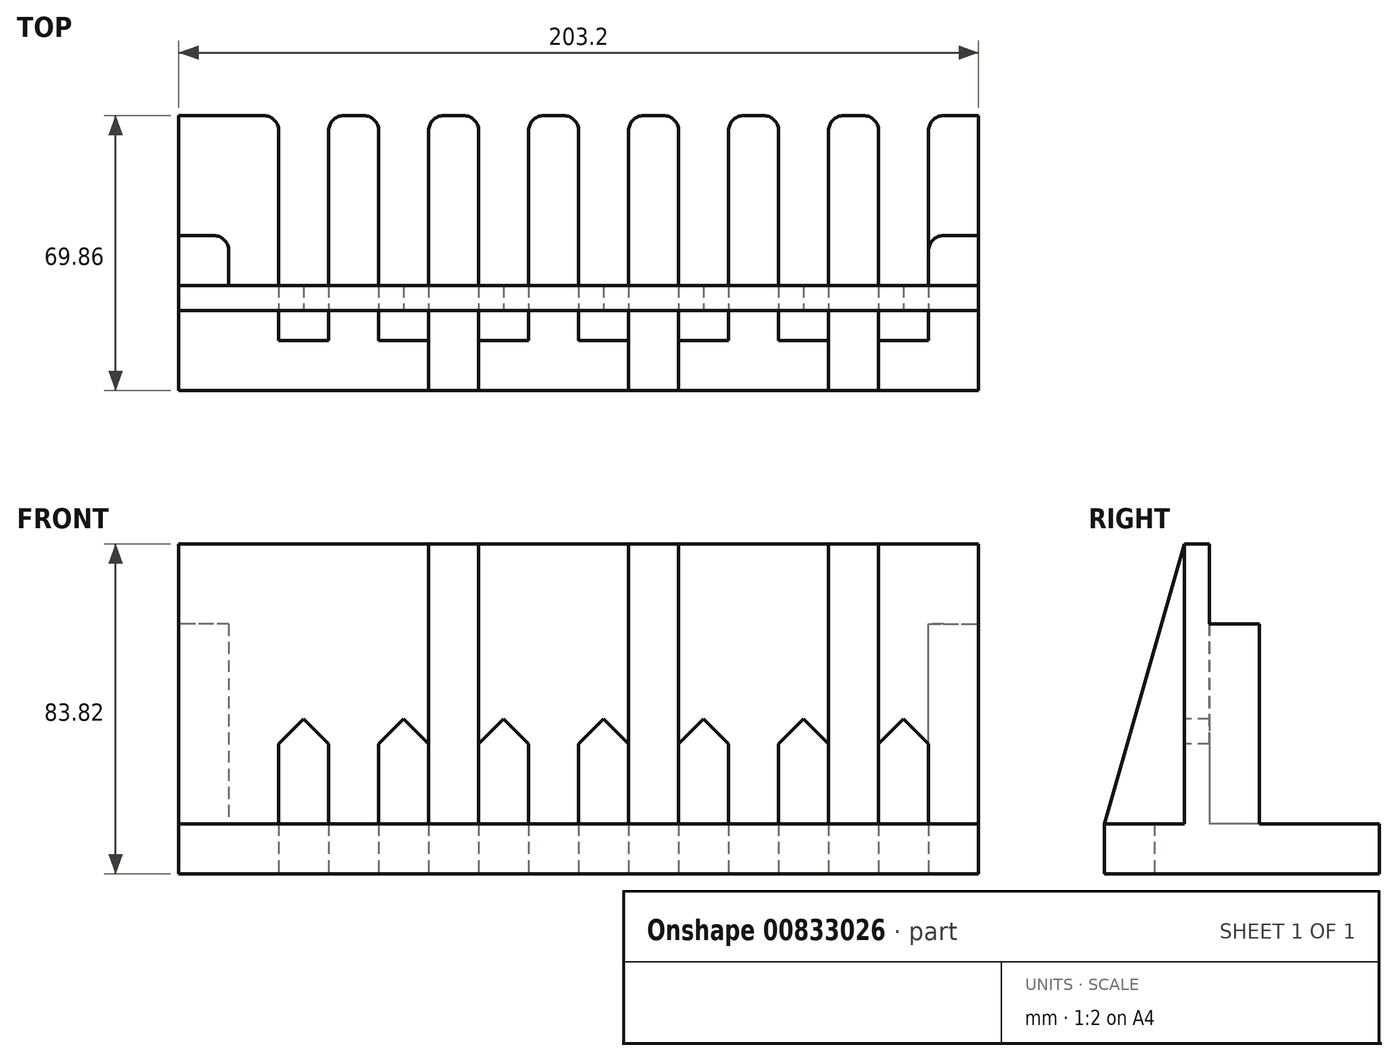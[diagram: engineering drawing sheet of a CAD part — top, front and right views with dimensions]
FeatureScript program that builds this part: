
annotation { "Feature Type Name" : "Feature", "Feature Type Description" : "" }
export const myFeature = defineFeature(function(context is Context, id is Id, definition is map)
    precondition{}
    {
        {
            var Q0;
            Q0=qCreatedBy(makeId("Top.planeOp"),FACE);
            var sketch = newSketch(context, id + "F0", { "sketchPlane" : qUnion([Q0])});
            skLineSegment(sketch, "E0.bottom", {"start": v(101.6, 34.93) * mm, "end": v(88.9, 34.93) * mm});
            skLineSegment(sketch, "E0.top", {"start": v(101.6, -34.92) * mm, "end": v(-101.6, -34.93) * mm});
            skLineSegment(sketch, "E0.left", {"start": v(101.6, 34.93) * mm, "end": v(101.6, -34.92) * mm});
            skLineSegment(sketch, "E0.right", {"start": v(-101.6, 34.92) * mm, "end": v(-101.6, -34.93) * mm});
            skPoint(sketch, "E0.middle", {"position": v(0, 0) * mm});
            skLineSegment(sketch, "E1.top", {"start": v(88.9, -22.23) * mm, "end": v(76.2, -22.23) * mm});
            skLineSegment(sketch, "E1.left", {"start": v(88.9, 34.93) * mm, "end": v(88.9, -22.23) * mm});
            skLineSegment(sketch, "E1.right", {"start": v(76.2, 34.93) * mm, "end": v(76.2, -22.23) * mm});
            skLineSegment(sketch, "E2.top", {"start": v(63.5, -22.23) * mm, "end": v(50.8, -22.23) * mm});
            skLineSegment(sketch, "E2.left", {"start": v(63.5, 34.93) * mm, "end": v(63.5, -22.23) * mm});
            skLineSegment(sketch, "E2.right", {"start": v(50.8, 34.93) * mm, "end": v(50.8, -22.23) * mm});
            skLineSegment(sketch, "E3.top", {"start": v(38.1, -22.22) * mm, "end": v(25.4, -22.22) * mm});
            skLineSegment(sketch, "E3.left", {"start": v(38.1, 34.93) * mm, "end": v(38.1, -22.22) * mm});
            skLineSegment(sketch, "E3.right", {"start": v(25.4, 34.93) * mm, "end": v(25.4, -22.23) * mm});
            skLineSegment(sketch, "E4.trimOffspring", {"start": v(50.8, 34.93) * mm, "end": v(38.1, 34.93) * mm});
            skLineSegment(sketch, "E5.trimOffspring", {"start": v(25.4, 34.93) * mm, "end": v(12.7, 34.93) * mm});
            skLineSegment(sketch, "E6.trimOffspring", {"start": v(76.2, 34.93) * mm, "end": v(63.5, 34.93) * mm});
            skLineSegment(sketch, "E7.top", {"start": v(12.7, -22.22) * mm, "end": v(0, -22.23) * mm});
            skLineSegment(sketch, "E7.left", {"start": v(12.7, 34.93) * mm, "end": v(12.7, -22.22) * mm});
            skLineSegment(sketch, "E7.right", {"start": v(0, 34.93) * mm, "end": v(0, -22.23) * mm});
            skLineSegment(sketch, "E8.top", {"start": v(-12.7, -22.22) * mm, "end": v(-25.4, -22.23) * mm});
            skLineSegment(sketch, "E8.left", {"start": v(-12.7, 34.93) * mm, "end": v(-12.7, -22.23) * mm});
            skLineSegment(sketch, "E8.right", {"start": v(-25.4, 34.93) * mm, "end": v(-25.4, -22.23) * mm});
            skLineSegment(sketch, "E9.top", {"start": v(-38.1, -22.22) * mm, "end": v(-50.8, -22.23) * mm});
            skLineSegment(sketch, "E9.left", {"start": v(-38.1, 34.93) * mm, "end": v(-38.1, -22.22) * mm});
            skLineSegment(sketch, "E9.right", {"start": v(-50.8, 34.92) * mm, "end": v(-50.8, -22.23) * mm});
            skLineSegment(sketch, "E10.trimOffspring", {"start": v(0, 34.93) * mm, "end": v(-12.7, 34.93) * mm});
            skLineSegment(sketch, "E11.trimOffspring", {"start": v(-25.4, 34.93) * mm, "end": v(-38.1, 34.93) * mm});
            skLineSegment(sketch, "E12.trimOffspring", {"start": v(-50.8, 34.92) * mm, "end": v(-63.5, 34.92) * mm});
            skLineSegment(sketch, "E13.bottom", {"start": v(-101.6, 34.92) * mm, "end": v(-88.9, 34.92) * mm});
            skLineSegment(sketch, "E13.top", {"start": v(-101.6, -22.23) * mm, "end": v(-88.9, -22.22) * mm});
            skLineSegment(sketch, "E13.left", {"start": v(-101.6, 34.92) * mm, "end": v(-101.6, -22.23) * mm});
            skLineSegment(sketch, "E13.right", {"start": v(-88.9, 34.92) * mm, "end": v(-88.9, -22.22) * mm});
            skLineSegment(sketch, "E14.top", {"start": v(-63.5, -22.22) * mm, "end": v(-76.2, -22.22) * mm});
            skLineSegment(sketch, "E14.left", {"start": v(-63.5, 34.92) * mm, "end": v(-63.5, -22.22) * mm});
            skLineSegment(sketch, "E14.right", {"start": v(-76.2, 34.92) * mm, "end": v(-76.2, -22.22) * mm});
            skLineSegment(sketch, "E15.trimOffspring", {"start": v(-76.2, 34.92) * mm, "end": v(-101.6, 34.92) * mm});
            skSolve(sketch);
        }
        {
            var Q0;
            Q0=makeQuery(id+"F0.imprint","IMPRINT",FACE,{"disambiguationData":[TD([[makeQuery(id+"F0.imprint","IMPRINT",EDGE,{"derivedFrom":sQuery(id+"F0.wireOp",EDGE,"E0.bottom")}),1.0]])]});
            var Q1;
            Q1=makeQuery(id+"F0.imprint","IMPRINT",FACE,{"disambiguationData":[TD([[makeQuery(id+"F0.imprint","IMPRINT",EDGE,{"derivedFrom":sQuery(id+"F0.wireOp",EDGE,"E13.top")}),1.0]])]});
            extrude(context, id + "F1", {"entities" : qUnion([Q0, Q1]), "depth" : 12.7 * mm, "offsetDistance" : 25.4 * mm});
        }
        {
            var Q0;
            Q0=makeQuery(id+"F1.opExtrude","CAP_FACE",FACE,{"disambiguationData":[OSD([sQuery(id+"F0.wireOp",EDGE,"E0.bottom"),sQuery(id+"F0.wireOp",EDGE,"E0.top"),sQuery(id+"F0.wireOp",EDGE,"E0.left"),sQuery(id+"F0.wireOp",EDGE,"E0.right"),sQuery(id+"F0.wireOp",EDGE,"E1.top"),sQuery(id+"F0.wireOp",EDGE,"E1.left"),sQuery(id+"F0.wireOp",EDGE,"E1.right"),sQuery(id+"F0.wireOp",EDGE,"E2.top"),sQuery(id+"F0.wireOp",EDGE,"E2.left"),sQuery(id+"F0.wireOp",EDGE,"E2.right"),sQuery(id+"F0.wireOp",EDGE,"E3.top"),sQuery(id+"F0.wireOp",EDGE,"E3.left"),sQuery(id+"F0.wireOp",EDGE,"E3.right"),sQuery(id+"F0.wireOp",EDGE,"E4.trimOffspring"),sQuery(id+"F0.wireOp",EDGE,"E5.trimOffspring"),sQuery(id+"F0.wireOp",EDGE,"E6.trimOffspring"),sQuery(id+"F0.wireOp",EDGE,"E7.top"),sQuery(id+"F0.wireOp",EDGE,"E7.left"),sQuery(id+"F0.wireOp",EDGE,"E7.right"),sQuery(id+"F0.wireOp",EDGE,"E8.top"),sQuery(id+"F0.wireOp",EDGE,"E8.left"),sQuery(id+"F0.wireOp",EDGE,"E8.right"),sQuery(id+"F0.wireOp",EDGE,"E9.top"),sQuery(id+"F0.wireOp",EDGE,"E9.left"),sQuery(id+"F0.wireOp",EDGE,"E9.right"),sQuery(id+"F0.wireOp",EDGE,"E10.trimOffspring"),sQuery(id+"F0.wireOp",EDGE,"E11.trimOffspring"),sQuery(id+"F0.wireOp",EDGE,"E12.trimOffspring")])],"isStart":false});
            var sketch = newSketch(context, id + "F2", { "sketchPlane" : qUnion([Q0])});
            skLineSegment(sketch, "E16.bottom", {"start": v(-101.6, -8.26) * mm, "end": v(101.6, -8.25) * mm});
            skLineSegment(sketch, "E16.top", {"start": v(-101.6, -14.6) * mm, "end": v(101.6, -14.6) * mm});
            skLineSegment(sketch, "E16.left", {"start": v(-101.6, -8.26) * mm, "end": v(-101.6, -14.6) * mm});
            skLineSegment(sketch, "E16.right", {"start": v(101.6, -8.25) * mm, "end": v(101.6, -14.6) * mm});
            skSolve(sketch);
        }
        {
            var Q0;
            {var subQ0=sQuery(id+"F2.wireOp",EDGE,"E16.left");Q0=makeQuery(id+"F2.imprint","IMPRINT",FACE,{"disambiguationData":[TD([[makeQuery(id+"F2.imprint","IMPRINT",EDGE,{"derivedFrom":subQ0}),1.0]])]});}
            var Q1;
            {var subQ0=sQuery(id+"F2.wireOp",EDGE,"E16.bottom");var subQ1=makeQuery(id+"F1.opExtrude","CAP_EDGE",EDGE,{"disambiguationData":[OSD([sQuery(id+"F0.wireOp",EDGE,"E9.left")])],"isStart":false});var subQ2=makeQuery(id+"F2.imprint","INTERSECT",VERTEX,{"derivedFrom":[subQ1,subQ0]});Q1=makeQuery(id+"F2.imprint","IMPRINT",FACE,{"disambiguationData":[TD([[makeQuery(id+"F2.imprint","IMPRINT",EDGE,{"disambiguationData":[TD([[subQ2,-1.0]])],"derivedFrom":subQ0}),-1.0]])]});}
            var Q2;
            {var subQ0=sQuery(id+"F2.wireOp",EDGE,"E16.bottom");var subQ1=makeQuery(id+"F1.opExtrude","CAP_EDGE",EDGE,{"disambiguationData":[OSD([sQuery(id+"F0.wireOp",EDGE,"E8.left")])],"isStart":false});var subQ2=makeQuery(id+"F2.imprint","INTERSECT",VERTEX,{"derivedFrom":[subQ1,subQ0]});Q2=makeQuery(id+"F2.imprint","IMPRINT",FACE,{"disambiguationData":[TD([[makeQuery(id+"F2.imprint","IMPRINT",EDGE,{"disambiguationData":[TD([[subQ2,-1.0]])],"derivedFrom":subQ0}),-1.0]])]});}
            var Q3;
            {var subQ0=sQuery(id+"F2.wireOp",EDGE,"E16.bottom");var subQ1=makeQuery(id+"F1.opExtrude","CAP_EDGE",EDGE,{"disambiguationData":[OSD([sQuery(id+"F0.wireOp",EDGE,"E7.left")])],"isStart":false});var subQ2=makeQuery(id+"F2.imprint","INTERSECT",VERTEX,{"derivedFrom":[subQ1,subQ0]});Q3=makeQuery(id+"F2.imprint","IMPRINT",FACE,{"disambiguationData":[TD([[makeQuery(id+"F2.imprint","IMPRINT",EDGE,{"disambiguationData":[TD([[subQ2,-1.0]])],"derivedFrom":subQ0}),-1.0]])]});}
            var Q4;
            {var subQ0=sQuery(id+"F2.wireOp",EDGE,"E16.bottom");var subQ1=makeQuery(id+"F1.opExtrude","CAP_EDGE",EDGE,{"disambiguationData":[OSD([sQuery(id+"F0.wireOp",EDGE,"E3.left")])],"isStart":false});var subQ2=makeQuery(id+"F2.imprint","INTERSECT",VERTEX,{"derivedFrom":[subQ1,subQ0]});Q4=makeQuery(id+"F2.imprint","IMPRINT",FACE,{"disambiguationData":[TD([[makeQuery(id+"F2.imprint","IMPRINT",EDGE,{"disambiguationData":[TD([[subQ2,-1.0]])],"derivedFrom":subQ0}),-1.0]])]});}
            var Q5;
            {var subQ0=sQuery(id+"F2.wireOp",EDGE,"E16.bottom");var subQ1=makeQuery(id+"F1.opExtrude","CAP_EDGE",EDGE,{"disambiguationData":[OSD([sQuery(id+"F0.wireOp",EDGE,"E2.left")])],"isStart":false});var subQ2=makeQuery(id+"F2.imprint","INTERSECT",VERTEX,{"derivedFrom":[subQ1,subQ0]});Q5=makeQuery(id+"F2.imprint","IMPRINT",FACE,{"disambiguationData":[TD([[makeQuery(id+"F2.imprint","IMPRINT",EDGE,{"disambiguationData":[TD([[subQ2,-1.0]])],"derivedFrom":subQ0}),-1.0]])]});}
            var Q6;
            {var subQ0=sQuery(id+"F2.wireOp",EDGE,"E16.right");Q6=makeQuery(id+"F2.imprint","IMPRINT",FACE,{"disambiguationData":[TD([[makeQuery(id+"F2.imprint","IMPRINT",EDGE,{"derivedFrom":subQ0}),-1.0]])]});}
            var Q7;
            {var subQ0=sQuery(id+"F2.wireOp",EDGE,"E16.bottom");var subQ1=makeQuery(id+"F1.opExtrude","CAP_EDGE",EDGE,{"disambiguationData":[OSD([sQuery(id+"F0.wireOp",EDGE,"E14.left")])],"isStart":false});var subQ2=makeQuery(id+"F2.imprint","INTERSECT",VERTEX,{"derivedFrom":[subQ1,subQ0]});Q7=makeQuery(id+"F2.imprint","IMPRINT",FACE,{"disambiguationData":[TD([[makeQuery(id+"F2.imprint","IMPRINT",EDGE,{"disambiguationData":[TD([[subQ2,-1.0]])],"derivedFrom":subQ0}),-1.0]])]});}
            extrude(context, id + "F3", {"entities" : qUnion([Q0, Q1, Q2, Q3, Q4, Q5, Q6, Q7]), "operationType" : NewBodyOperationType.ADD, "depth" : 20.32 * mm, "offsetDistance" : 25.4 * mm});
        }
        {
            var Q0;
            Q0=makeQuery(id+"F3.opExtrude","CAP_FACE",FACE,{"disambiguationData":[OSD([sQuery(id+"F0.wireOp",EDGE,"E9.right"),sQuery(id+"F2.wireOp",EDGE,"E16.bottom"),sQuery(id+"F2.wireOp",EDGE,"E16.top"),sQuery(id+"F2.wireOp",EDGE,"E16.left")])],"isStart":false});
            var sketch = newSketch(context, id + "F4", { "sketchPlane" : qUnion([Q0])});
            skLineSegment(sketch, "E17.bottom", {"start": v(-101.6, -8.25) * mm, "end": v(101.6, -8.25) * mm});
            skLineSegment(sketch, "E17.top", {"start": v(-101.6, -14.6) * mm, "end": v(101.6, -14.6) * mm});
            skLineSegment(sketch, "E17.left", {"start": v(-101.6, -8.25) * mm, "end": v(-101.6, -14.6) * mm});
            skLineSegment(sketch, "E17.right", {"start": v(101.6, -8.25) * mm, "end": v(101.6, -14.6) * mm});
            skSolve(sketch);
        }
        {
            var Q0;
            {var subQ0=sQuery(id+"F4.wireOp",EDGE,"E17.left");Q0=makeQuery(id+"F4.imprint","IMPRINT",FACE,{"disambiguationData":[TD([[makeQuery(id+"F4.imprint","IMPRINT",EDGE,{"derivedFrom":subQ0}),1.0]])]});}
            var Q1;
            {var subQ2=sQuery(id+"F4.wireOp",EDGE,"E17.right");Q1=makeQuery(id+"F4.imprint","IMPRINT",FACE,{"disambiguationData":[TD([[makeQuery(id+"F4.imprint","IMPRINT",EDGE,{"derivedFrom":subQ2}),-1.0]])]});}
            var Q2;
            {var subQ2=makeQuery(id+"F3.opExtrude","CAP_EDGE",EDGE,{"disambiguationData":[OSD([sQuery(id+"F0.wireOp",EDGE,"E9.right")])],"isStart":false});Q2=makeQuery(id+"F4.imprint","IMPRINT",FACE,{"disambiguationData":[TD([[makeQuery(id+"F4.imprint","IMPRINT",EDGE,{"derivedFrom":subQ2}),-1.0]])]});}
            var Q3;
            {var subQ2=makeQuery(id+"F3.opExtrude","CAP_EDGE",EDGE,{"disambiguationData":[OSD([sQuery(id+"F0.wireOp",EDGE,"E14.left")])],"isStart":false});Q3=makeQuery(id+"F4.imprint","IMPRINT",FACE,{"disambiguationData":[TD([[makeQuery(id+"F4.imprint","IMPRINT",EDGE,{"derivedFrom":subQ2}),-1.0]])]});}
            extrude(context, id + "F5", {"entities" : qUnion([Q0, Q1, Q2, Q3]), "operationType" : NewBodyOperationType.ADD, "depth" : 50.8 * mm, "offsetDistance" : 25.4 * mm});
        }
        {
            var Q0;
            Q0=makeQuery(id+"F5.boolean.opBoolean","MERGE",FACE,{"derivedFrom":[makeQuery(id+"F3.boolean.opBoolean","MERGE",FACE,{"derivedFrom":[makeQuery(id+"F1.opExtrude","SWEPT_FACE",FACE,{"disambiguationData":[OSD([sQuery(id+"F0.wireOp",EDGE,"E0.right")])]}),makeQuery(id+"F3.opExtrude","SWEPT_FACE",FACE,{"disambiguationData":[OSD([sQuery(id+"F2.wireOp",EDGE,"E16.left")])]})]}),makeQuery(id+"F5.opExtrude","SWEPT_FACE",FACE,{"disambiguationData":[OSD([sQuery(id+"F4.wireOp",EDGE,"E17.left")])]})]});
            var sketch = newSketch(context, id + "F6", { "sketchPlane" : qUnion([Q0])});
            skLineSegment(sketch, "E18.bottom", {"start": v(8.25, 12.7) * mm, "end": v(-4.45, 12.7) * mm});
            skLineSegment(sketch, "E18.top", {"start": v(8.25, 63.5) * mm, "end": v(-4.45, 63.5) * mm});
            skLineSegment(sketch, "E18.left", {"start": v(8.25, 12.7) * mm, "end": v(8.25, 63.5) * mm});
            skLineSegment(sketch, "E18.right", {"start": v(-4.45, 12.7) * mm, "end": v(-4.45, 63.5) * mm});
            skSolve(sketch);
        }
        {
            var Q0;
            Q0=makeQuery(id+"F6.imprint","IMPRINT",FACE,{"disambiguationData":[TD([[makeQuery(id+"F6.imprint","IMPRINT",EDGE,{"derivedFrom":sQuery(id+"F6.wireOp",EDGE,"E18.bottom")}),1.0]])]});
            var Q1;
            Q1=makeQuery(id+"F6.imprint","IMPRINT",FACE,{"disambiguationData":[TD([[makeQuery(id+"F6.imprint","IMPRINT",EDGE,{"derivedFrom":sQuery(id+"F6.wireOp",EDGE,"ogDCGRYY-HDVT-Hkr0-qh3N-PnepQPiMfiLJ")}),-1.0]])]});
            extrude(context, id + "F7", {"entities" : qUnion([Q0, Q1]), "operationType" : NewBodyOperationType.ADD, "oppositeDirection" : true, "depth" : 12.7 * mm, "offsetDistance" : 25.4 * mm});
        }
        {
            var Q0;
            {var subQ0=sQuery(id+"F0.wireOp",EDGE,"E8.right");Q0=makeQuery(id+"F3.boolean.opBoolean","MERGE",FACE,{"derivedFrom":[makeQuery(id+"F1.opExtrude","SWEPT_FACE",FACE,{"disambiguationData":[OSD([subQ0])]}),makeQuery(id+"F3.opExtrude","SWEPT_FACE",FACE,{"disambiguationData":[OSD([subQ0])]})]});}
            var sketch = newSketch(context, id + "F8", { "sketchPlane" : qUnion([Q0])});
            skLineSegment(sketch, "E19", {"start": v(-14.6, 83.82) * mm, "end": v(-34.93, 12.7) * mm});
            skLineSegment(sketch, "E20", {"start": v(-34.92, 12.7) * mm, "end": v(-14.6, 12.7) * mm});
            skLineSegment(sketch, "E21", {"start": v(-14.6, 12.7) * mm, "end": v(-14.6, 83.82) * mm});
            skSolve(sketch);
        }
        {
            var Q0;
            {var subQ3=sQuery(id+"F8.wireOp",EDGE,"E19");Q0=makeQuery(id+"F8.imprint","IMPRINT",FACE,{"disambiguationData":[TD([[makeQuery(id+"F8.imprint","IMPRINT",EDGE,{"derivedFrom":subQ3}),1.0]])]});}
            var Q1;
            {var subQ0=sQuery(id+"F0.wireOp",EDGE,"E9.left");Q1=makeQuery(id+"F3.boolean.opBoolean","MERGE",FACE,{"derivedFrom":[makeQuery(id+"F1.opExtrude","SWEPT_FACE",FACE,{"disambiguationData":[OSD([subQ0])]}),makeQuery(id+"F3.opExtrude","SWEPT_FACE",FACE,{"disambiguationData":[OSD([subQ0])]})]});}
            extrude(context, id + "F9", {"entities" : qUnion([Q0]), "operationType" : NewBodyOperationType.ADD, "endBound" : BoundingType.UP_TO_SURFACE, "oppositeDirection" : true, "depth" : 25.4 * mm, "endBoundEntityFace" : qUnion([Q1]), "offsetDistance" : 25.4 * mm});
        }
        {
            var Q0;
            {var subQ0=sQuery(id+"F0.wireOp",EDGE,"E3.right");Q0=makeQuery(id+"F3.boolean.opBoolean","MERGE",FACE,{"derivedFrom":[makeQuery(id+"F1.opExtrude","SWEPT_FACE",FACE,{"disambiguationData":[OSD([subQ0])]}),makeQuery(id+"F3.opExtrude","SWEPT_FACE",FACE,{"disambiguationData":[OSD([subQ0])]})]});}
            var sketch = newSketch(context, id + "F10", { "sketchPlane" : qUnion([Q0])});
            skLineSegment(sketch, "E22", {"start": v(-14.6, 83.82) * mm, "end": v(-34.93, 12.7) * mm});
            skLineSegment(sketch, "E23", {"start": v(-34.92, 12.7) * mm, "end": v(-14.6, 12.7) * mm});
            skLineSegment(sketch, "E24", {"start": v(-14.6, 12.7) * mm, "end": v(-14.6, 83.82) * mm});
            skSolve(sketch);
        }
        {
            var Q0;
            {var subQ3=sQuery(id+"F10.wireOp",EDGE,"E22");Q0=makeQuery(id+"F10.imprint","IMPRINT",FACE,{"disambiguationData":[TD([[makeQuery(id+"F10.imprint","IMPRINT",EDGE,{"derivedFrom":subQ3}),1.0]])]});}
            var Q1;
            {var subQ0=sQuery(id+"F0.wireOp",EDGE,"E7.left");Q1=makeQuery(id+"F3.boolean.opBoolean","MERGE",FACE,{"derivedFrom":[makeQuery(id+"F1.opExtrude","SWEPT_FACE",FACE,{"disambiguationData":[OSD([subQ0])]}),makeQuery(id+"F3.opExtrude","SWEPT_FACE",FACE,{"disambiguationData":[OSD([subQ0])]})]});}
            extrude(context, id + "F11", {"entities" : qUnion([Q0]), "operationType" : NewBodyOperationType.ADD, "endBound" : BoundingType.UP_TO_SURFACE, "oppositeDirection" : true, "depth" : 25.4 * mm, "endBoundEntityFace" : qUnion([Q1]), "offsetDistance" : 25.4 * mm});
        }
        {
            var Q0;
            {var subQ0=sQuery(id+"F0.wireOp",EDGE,"E1.right");Q0=makeQuery(id+"F3.boolean.opBoolean","MERGE",FACE,{"derivedFrom":[makeQuery(id+"F1.opExtrude","SWEPT_FACE",FACE,{"disambiguationData":[OSD([subQ0])]}),makeQuery(id+"F3.opExtrude","SWEPT_FACE",FACE,{"disambiguationData":[OSD([subQ0])]})]});}
            var sketch = newSketch(context, id + "F12", { "sketchPlane" : qUnion([Q0])});
            skLineSegment(sketch, "E25", {"start": v(-14.6, 83.82) * mm, "end": v(-14.6, 12.7) * mm});
            skLineSegment(sketch, "E26", {"start": v(-14.6, 12.7) * mm, "end": v(-34.93, 12.7) * mm});
            skLineSegment(sketch, "E27", {"start": v(-34.93, 12.7) * mm, "end": v(-14.6, 83.82) * mm});
            skSolve(sketch);
        }
        {
            var Q0;
            {var subQ5=sQuery(id+"F12.wireOp",EDGE,"E27");Q0=makeQuery(id+"F12.imprint","IMPRINT",FACE,{"disambiguationData":[TD([[makeQuery(id+"F12.imprint","IMPRINT",EDGE,{"derivedFrom":subQ5}),-1.0]])]});}
            var Q1;
            {var subQ0=sQuery(id+"F0.wireOp",EDGE,"E2.left");Q1=makeQuery(id+"F3.boolean.opBoolean","MERGE",FACE,{"derivedFrom":[makeQuery(id+"F1.opExtrude","SWEPT_FACE",FACE,{"disambiguationData":[OSD([subQ0])]}),makeQuery(id+"F3.opExtrude","SWEPT_FACE",FACE,{"disambiguationData":[OSD([subQ0])]})]});}
            extrude(context, id + "F13", {"entities" : qUnion([Q0]), "operationType" : NewBodyOperationType.ADD, "endBound" : BoundingType.UP_TO_SURFACE, "oppositeDirection" : true, "depth" : 25.4 * mm, "endBoundEntityFace" : qUnion([Q1]), "offsetDistance" : 25.4 * mm});
        }
        {
            var Q0;
            Q0=makeQuery(id+"F5.boolean.opBoolean","MERGE",FACE,{"derivedFrom":[makeQuery(id+"F3.boolean.opBoolean","MERGE",FACE,{"derivedFrom":[makeQuery(id+"F1.opExtrude","SWEPT_FACE",FACE,{"disambiguationData":[OSD([sQuery(id+"F0.wireOp",EDGE,"E0.left")])]}),makeQuery(id+"F3.opExtrude","SWEPT_FACE",FACE,{"disambiguationData":[OSD([sQuery(id+"F2.wireOp",EDGE,"E16.right")])]})]}),makeQuery(id+"F5.opExtrude","SWEPT_FACE",FACE,{"disambiguationData":[OSD([sQuery(id+"F4.wireOp",EDGE,"E17.right")])]})]});
            var sketch = newSketch(context, id + "F14", { "sketchPlane" : qUnion([Q0])});
            skLineSegment(sketch, "E28.bottom", {"start": v(4.45, 63.5) * mm, "end": v(-8.26, 63.5) * mm});
            skLineSegment(sketch, "E28.top", {"start": v(4.45, 12.7) * mm, "end": v(-8.26, 12.7) * mm});
            skLineSegment(sketch, "E28.left", {"start": v(4.45, 63.5) * mm, "end": v(4.45, 12.7) * mm});
            skLineSegment(sketch, "E28.right", {"start": v(-8.26, 63.5) * mm, "end": v(-8.26, 12.7) * mm});
            skSolve(sketch);
        }
        {
            var Q0;
            Q0=makeQuery(id+"F14.imprint","IMPRINT",FACE,{"disambiguationData":[TD([[makeQuery(id+"F14.imprint","IMPRINT",EDGE,{"derivedFrom":sQuery(id+"F14.wireOp",EDGE,"E28.bottom")}),1.0]])]});
            var Q1;
            {var subQ0=sQuery(id+"F0.wireOp",EDGE,"E1.left");Q1=makeQuery(id+"F3.boolean.opBoolean","MERGE",FACE,{"derivedFrom":[makeQuery(id+"F1.opExtrude","SWEPT_FACE",FACE,{"disambiguationData":[OSD([subQ0])]}),makeQuery(id+"F3.opExtrude","SWEPT_FACE",FACE,{"disambiguationData":[OSD([subQ0])]})]});}
            extrude(context, id + "F15", {"entities" : qUnion([Q0]), "operationType" : NewBodyOperationType.ADD, "endBound" : BoundingType.UP_TO_SURFACE, "oppositeDirection" : true, "depth" : 25.4 * mm, "endBoundEntityFace" : qUnion([Q1]), "offsetDistance" : 25.4 * mm});
        }
        {
            var Q0;
            Q0=makeQuery(id+"F1.opExtrude","SWEPT_EDGE",EDGE,{"disambiguationData":[OSD([sQuery(id+"F0.wireOp",EDGE,"E0.bottom"),sQuery(id+"F0.wireOp",EDGE,"E1.left")])]});
            var Q1;
            Q1=makeQuery(id+"F1.opExtrude","SWEPT_EDGE",EDGE,{"disambiguationData":[OSD([sQuery(id+"F0.wireOp",EDGE,"E2.left"),sQuery(id+"F0.wireOp",EDGE,"E6.trimOffspring")])]});
            var Q2;
            Q2=makeQuery(id+"F1.opExtrude","SWEPT_EDGE",EDGE,{"disambiguationData":[OSD([sQuery(id+"F0.wireOp",EDGE,"E3.left"),sQuery(id+"F0.wireOp",EDGE,"E4.trimOffspring")])]});
            var Q3;
            Q3=makeQuery(id+"F1.opExtrude","SWEPT_EDGE",EDGE,{"disambiguationData":[OSD([sQuery(id+"F0.wireOp",EDGE,"E5.trimOffspring"),sQuery(id+"F0.wireOp",EDGE,"E7.left")])]});
            var Q4;
            Q4=makeQuery(id+"F1.opExtrude","SWEPT_EDGE",EDGE,{"disambiguationData":[OSD([sQuery(id+"F0.wireOp",EDGE,"E8.left"),sQuery(id+"F0.wireOp",EDGE,"E10.trimOffspring")])]});
            var Q5;
            Q5=makeQuery(id+"F1.opExtrude","SWEPT_EDGE",EDGE,{"disambiguationData":[OSD([sQuery(id+"F0.wireOp",EDGE,"E9.left"),sQuery(id+"F0.wireOp",EDGE,"E11.trimOffspring")])]});
            var Q6;
            Q6=makeQuery(id+"F1.opExtrude","SWEPT_EDGE",EDGE,{"disambiguationData":[OSD([sQuery(id+"F0.wireOp",EDGE,"E1.right"),sQuery(id+"F0.wireOp",EDGE,"E6.trimOffspring")])]});
            var Q7;
            Q7=makeQuery(id+"F1.opExtrude","SWEPT_EDGE",EDGE,{"disambiguationData":[OSD([sQuery(id+"F0.wireOp",EDGE,"E2.right"),sQuery(id+"F0.wireOp",EDGE,"E4.trimOffspring")])]});
            var Q8;
            Q8=makeQuery(id+"F1.opExtrude","SWEPT_EDGE",EDGE,{"disambiguationData":[OSD([sQuery(id+"F0.wireOp",EDGE,"E3.right"),sQuery(id+"F0.wireOp",EDGE,"E5.trimOffspring")])]});
            var Q9;
            Q9=makeQuery(id+"F1.opExtrude","SWEPT_EDGE",EDGE,{"disambiguationData":[OSD([sQuery(id+"F0.wireOp",EDGE,"E7.right"),sQuery(id+"F0.wireOp",EDGE,"E10.trimOffspring")])]});
            var Q10;
            Q10=makeQuery(id+"F1.opExtrude","SWEPT_EDGE",EDGE,{"disambiguationData":[OSD([sQuery(id+"F0.wireOp",EDGE,"E8.right"),sQuery(id+"F0.wireOp",EDGE,"E11.trimOffspring")])]});
            var Q11;
            Q11=makeQuery(id+"F1.opExtrude","SWEPT_EDGE",EDGE,{"disambiguationData":[OSD([sQuery(id+"F0.wireOp",EDGE,"E9.right"),sQuery(id+"F0.wireOp",EDGE,"E12.trimOffspring")])]});
            var Q12;
            Q12=makeQuery(id+"F1.opExtrude","SWEPT_EDGE",EDGE,{"disambiguationData":[OSD([sQuery(id+"F0.wireOp",EDGE,"E14.right"),sQuery(id+"F0.wireOp",EDGE,"E15.trimOffspring")])]});
            var Q13;
            Q13=makeQuery(id+"F1.opExtrude","SWEPT_EDGE",EDGE,{"disambiguationData":[OSD([sQuery(id+"F0.wireOp",EDGE,"E12.trimOffspring"),sQuery(id+"F0.wireOp",EDGE,"E14.left")])]});
            fillet(context, id + "F16", {"entities" : qUnion([Q0, Q1, Q2, Q3, Q4, Q5, Q6, Q7, Q8, Q9, Q10, Q11, Q12, Q13]), "radius" : 3.8 * mm, "tangentPropagation" : true, "allowEdgeOverflow" : false});
        }
        {
            var Q0;
            {var subQ0=sQuery(id+"F0.wireOp",EDGE,"E9.left");var subQ1=sQuery(id+"F0.wireOp",EDGE,"E14.right");var subQ2=sQuery(id+"F0.wireOp",EDGE,"E14.left");var subQ6=sQuery(id+"F0.wireOp",EDGE,"E8.left");var subQ8=sQuery(id+"F0.wireOp",EDGE,"E7.left");var subQ10=sQuery(id+"F0.wireOp",EDGE,"E3.left");var subQ12=sQuery(id+"F0.wireOp",EDGE,"E2.left");var subQ14=sQuery(id+"F0.wireOp",EDGE,"E1.left");var subQ20=sQuery(id+"F4.wireOp",EDGE,"E17.top");var subQ23=sQuery(id+"F2.wireOp",EDGE,"E16.top");Q0=makeQuery(id+"F9.boolean.opBoolean","SPLIT",FACE,{"disambiguationData":[TD([makeQuery(id+"F1.opExtrude","SWEPT_FACE",FACE,{"disambiguationData":[OSD([subQ0])]})])],"derivedFrom":makeQuery(id+"F5.boolean.opBoolean","MERGE",FACE,{"derivedFrom":[makeQuery(id+"F3.opExtrude","SWEPT_FACE",FACE,{"disambiguationData":[OSD([subQ23]),TDD([makeQuery(id+"F2.imprint","IMPRINT",EDGE,{"disambiguationData":[TD([[makeQuery(id+"F2.imprint","INTERSECT",VERTEX,{"derivedFrom":[makeQuery(id+"F1.opExtrude","CAP_EDGE",EDGE,{"disambiguationData":[OSD([subQ1])],"isStart":false}),subQ23]}),1.0]])],"derivedFrom":subQ23})])]}),makeQuery(id+"F3.opExtrude","SWEPT_FACE",FACE,{"disambiguationData":[OSD([subQ23]),TDD([makeQuery(id+"F2.imprint","IMPRINT",EDGE,{"disambiguationData":[TD([[makeQuery(id+"F2.imprint","INTERSECT",VERTEX,{"derivedFrom":[makeQuery(id+"F1.opExtrude","CAP_EDGE",EDGE,{"disambiguationData":[OSD([subQ2])],"isStart":false}),subQ23]}),-1.0]])],"derivedFrom":subQ23})])]}),makeQuery(id+"F3.opExtrude","SWEPT_FACE",FACE,{"disambiguationData":[OSD([subQ23]),TDD([makeQuery(id+"F2.imprint","IMPRINT",EDGE,{"disambiguationData":[TD([[makeQuery(id+"F2.imprint","INTERSECT",VERTEX,{"derivedFrom":[makeQuery(id+"F1.opExtrude","CAP_EDGE",EDGE,{"disambiguationData":[OSD([subQ0])],"isStart":false}),subQ23]}),-1.0]])],"derivedFrom":subQ23})])]}),makeQuery(id+"F3.opExtrude","SWEPT_FACE",FACE,{"disambiguationData":[OSD([subQ23]),TDD([makeQuery(id+"F2.imprint","IMPRINT",EDGE,{"disambiguationData":[TD([[makeQuery(id+"F2.imprint","INTERSECT",VERTEX,{"derivedFrom":[makeQuery(id+"F1.opExtrude","CAP_EDGE",EDGE,{"disambiguationData":[OSD([subQ6])],"isStart":false}),subQ23]}),-1.0]])],"derivedFrom":subQ23})])]}),makeQuery(id+"F3.opExtrude","SWEPT_FACE",FACE,{"disambiguationData":[OSD([subQ23]),TDD([makeQuery(id+"F2.imprint","IMPRINT",EDGE,{"disambiguationData":[TD([[makeQuery(id+"F2.imprint","INTERSECT",VERTEX,{"derivedFrom":[makeQuery(id+"F1.opExtrude","CAP_EDGE",EDGE,{"disambiguationData":[OSD([subQ8])],"isStart":false}),subQ23]}),-1.0]])],"derivedFrom":subQ23})])]}),makeQuery(id+"F3.opExtrude","SWEPT_FACE",FACE,{"disambiguationData":[OSD([subQ23]),TDD([makeQuery(id+"F2.imprint","IMPRINT",EDGE,{"disambiguationData":[TD([[makeQuery(id+"F2.imprint","INTERSECT",VERTEX,{"derivedFrom":[makeQuery(id+"F1.opExtrude","CAP_EDGE",EDGE,{"disambiguationData":[OSD([subQ10])],"isStart":false}),subQ23]}),-1.0]])],"derivedFrom":subQ23})])]}),makeQuery(id+"F3.opExtrude","SWEPT_FACE",FACE,{"disambiguationData":[OSD([subQ23]),TDD([makeQuery(id+"F2.imprint","IMPRINT",EDGE,{"disambiguationData":[TD([[makeQuery(id+"F2.imprint","INTERSECT",VERTEX,{"derivedFrom":[makeQuery(id+"F1.opExtrude","CAP_EDGE",EDGE,{"disambiguationData":[OSD([subQ12])],"isStart":false}),subQ23]}),-1.0]])],"derivedFrom":subQ23})])]}),makeQuery(id+"F3.opExtrude","SWEPT_FACE",FACE,{"disambiguationData":[OSD([subQ23]),TDD([makeQuery(id+"F2.imprint","IMPRINT",EDGE,{"disambiguationData":[TD([[makeQuery(id+"F2.imprint","INTERSECT",VERTEX,{"derivedFrom":[makeQuery(id+"F1.opExtrude","CAP_EDGE",EDGE,{"disambiguationData":[OSD([subQ14])],"isStart":false}),subQ23]}),-1.0]])],"derivedFrom":subQ23})])]}),makeQuery(id+"F5.opExtrude","SWEPT_FACE",FACE,{"disambiguationData":[OSD([subQ20])]})]})});}
            var sketch = newSketch(context, id + "F17", { "sketchPlane" : qUnion([Q0])});
            skLineSegment(sketch, "E29.bottom", {"start": v(-50.8, 33.02) * mm, "end": v(-38.1, 33.02) * mm});
            skLineSegment(sketch, "E29.top", {"start": v(-50.8, 39.37) * mm, "end": v(-38.1, 39.37) * mm});
            skLineSegment(sketch, "E29.left", {"start": v(-50.8, 33.02) * mm, "end": v(-50.8, 39.37) * mm});
            skLineSegment(sketch, "E29.right", {"start": v(-38.1, 33.02) * mm, "end": v(-38.1, 39.37) * mm});
            skLineSegment(sketch, "E30.bottom", {"start": v(-12.7, 33.02) * mm, "end": v(-25.4, 33.02) * mm});
            skLineSegment(sketch, "E30.top", {"start": v(-12.7, 39.37) * mm, "end": v(-25.4, 39.37) * mm});
            skLineSegment(sketch, "E30.left", {"start": v(-12.7, 33.02) * mm, "end": v(-12.7, 39.37) * mm});
            skLineSegment(sketch, "E30.right", {"start": v(-25.4, 33.02) * mm, "end": v(-25.4, 39.37) * mm});
            skLineSegment(sketch, "E31.bottom", {"start": v(0, 33.02) * mm, "end": v(12.7, 33.02) * mm});
            skLineSegment(sketch, "E31.top", {"start": v(0, 39.37) * mm, "end": v(12.7, 39.37) * mm});
            skLineSegment(sketch, "E31.left", {"start": v(0, 33.02) * mm, "end": v(0, 39.37) * mm});
            skLineSegment(sketch, "E31.right", {"start": v(12.7, 33.02) * mm, "end": v(12.7, 39.37) * mm});
            skLineSegment(sketch, "E32.bottom", {"start": v(25.4, 33.02) * mm, "end": v(38.1, 33.02) * mm});
            skLineSegment(sketch, "E32.top", {"start": v(25.4, 39.37) * mm, "end": v(38.1, 39.37) * mm});
            skLineSegment(sketch, "E32.left", {"start": v(25.4, 33.02) * mm, "end": v(25.4, 39.37) * mm});
            skLineSegment(sketch, "E32.right", {"start": v(38.1, 33.02) * mm, "end": v(38.1, 39.37) * mm});
            skLineSegment(sketch, "E33.bottom", {"start": v(50.8, 33.02) * mm, "end": v(63.5, 33.02) * mm});
            skLineSegment(sketch, "E33.top", {"start": v(50.8, 39.37) * mm, "end": v(63.5, 39.37) * mm});
            skLineSegment(sketch, "E33.left", {"start": v(50.8, 33.02) * mm, "end": v(50.8, 39.37) * mm});
            skLineSegment(sketch, "E33.right", {"start": v(63.5, 33.02) * mm, "end": v(63.5, 39.37) * mm});
            skLineSegment(sketch, "E34.bottom", {"start": v(88.9, 33.02) * mm, "end": v(76.2, 33.02) * mm});
            skLineSegment(sketch, "E34.top", {"start": v(88.9, 39.37) * mm, "end": v(76.2, 39.37) * mm});
            skLineSegment(sketch, "E34.left", {"start": v(88.9, 33.02) * mm, "end": v(88.9, 39.37) * mm});
            skLineSegment(sketch, "E34.right", {"start": v(76.2, 33.02) * mm, "end": v(76.2, 39.37) * mm});
            skPoint(sketch, "E35", {"position": v(-44.45, 39.37) * mm});
            skPoint(sketch, "E36", {"position": v(-19.05, 39.37) * mm});
            skPoint(sketch, "E37", {"position": v(6.35, 39.37) * mm});
            skPoint(sketch, "E38", {"position": v(31.75, 39.37) * mm});
            skPoint(sketch, "E39", {"position": v(57.15, 39.37) * mm});
            skPoint(sketch, "E40", {"position": v(82.55, 39.37) * mm});
            skLineSegment(sketch, "E41", {"start": v(-50.8, 33.02) * mm, "end": v(-44.45, 39.37) * mm});
            skLineSegment(sketch, "E42", {"start": v(-38.1, 33.02) * mm, "end": v(-44.45, 39.37) * mm});
            skLineSegment(sketch, "E43", {"start": v(-19.05, 39.37) * mm, "end": v(-25.4, 33.02) * mm});
            skLineSegment(sketch, "E44", {"start": v(-19.05, 39.37) * mm, "end": v(-12.7, 33.02) * mm});
            skLineSegment(sketch, "E45", {"start": v(6.35, 39.37) * mm, "end": v(0, 33.02) * mm});
            skLineSegment(sketch, "E46", {"start": v(6.35, 39.37) * mm, "end": v(12.7, 33.02) * mm});
            skLineSegment(sketch, "E47", {"start": v(31.75, 39.37) * mm, "end": v(25.4, 33.02) * mm});
            skLineSegment(sketch, "E48", {"start": v(31.75, 39.37) * mm, "end": v(38.1, 33.02) * mm});
            skLineSegment(sketch, "E49", {"start": v(57.15, 39.37) * mm, "end": v(50.8, 33.02) * mm});
            skLineSegment(sketch, "E50", {"start": v(57.15, 39.37) * mm, "end": v(63.5, 33.02) * mm});
            skLineSegment(sketch, "E51", {"start": v(82.55, 39.37) * mm, "end": v(76.2, 33.02) * mm});
            skLineSegment(sketch, "E52", {"start": v(82.55, 39.37) * mm, "end": v(88.9, 33.02) * mm});
            skLineSegment(sketch, "E53.bottom", {"start": v(-63.5, 33.02) * mm, "end": v(-76.2, 33.02) * mm});
            skLineSegment(sketch, "E53.top", {"start": v(-63.5, 39.37) * mm, "end": v(-76.2, 39.37) * mm});
            skLineSegment(sketch, "E53.left", {"start": v(-63.5, 33.02) * mm, "end": v(-63.5, 39.37) * mm});
            skLineSegment(sketch, "E53.right", {"start": v(-76.2, 33.02) * mm, "end": v(-76.2, 39.37) * mm});
            skPoint(sketch, "E54", {"position": v(-69.85, 39.37) * mm});
            skLineSegment(sketch, "E55", {"start": v(-69.85, 39.37) * mm, "end": v(-63.5, 33.02) * mm});
            skLineSegment(sketch, "E56", {"start": v(-69.85, 39.37) * mm, "end": v(-76.2, 33.02) * mm});
            skSolve(sketch);
        }
        {
            var Q0;
            Q0=makeQuery(id+"F17.imprint","IMPRINT",FACE,{"disambiguationData":[TD([[makeQuery(id+"F17.imprint","IMPRINT",EDGE,{"derivedFrom":sQuery(id+"F17.wireOp",EDGE,"E29.bottom")}),1.0]])]});
            var Q1;
            Q1=makeQuery(id+"F17.imprint","IMPRINT",FACE,{"disambiguationData":[TD([[makeQuery(id+"F17.imprint","IMPRINT",EDGE,{"derivedFrom":sQuery(id+"F17.wireOp",EDGE,"E30.bottom")}),-1.0]])]});
            var Q2;
            Q2=makeQuery(id+"F17.imprint","IMPRINT",FACE,{"disambiguationData":[TD([[makeQuery(id+"F17.imprint","IMPRINT",EDGE,{"derivedFrom":sQuery(id+"F17.wireOp",EDGE,"E31.bottom")}),1.0]])]});
            var Q3;
            Q3=makeQuery(id+"F17.imprint","IMPRINT",FACE,{"disambiguationData":[TD([[makeQuery(id+"F17.imprint","IMPRINT",EDGE,{"derivedFrom":sQuery(id+"F17.wireOp",EDGE,"E32.bottom")}),1.0]])]});
            var Q4;
            Q4=makeQuery(id+"F17.imprint","IMPRINT",FACE,{"disambiguationData":[TD([[makeQuery(id+"F17.imprint","IMPRINT",EDGE,{"derivedFrom":sQuery(id+"F17.wireOp",EDGE,"E33.bottom")}),1.0]])]});
            var Q5;
            Q5=makeQuery(id+"F17.imprint","IMPRINT",FACE,{"disambiguationData":[TD([[makeQuery(id+"F17.imprint","IMPRINT",EDGE,{"derivedFrom":sQuery(id+"F17.wireOp",EDGE,"E34.bottom")}),-1.0]])]});
            var Q6;
            Q6=makeQuery(id+"F17.imprint","IMPRINT",FACE,{"disambiguationData":[TD([[makeQuery(id+"F17.imprint","IMPRINT",EDGE,{"derivedFrom":sQuery(id+"F17.wireOp",EDGE,"E53.bottom")}),1.0]])]});
            var Q7;
            {var subQ0=sQuery(id+"F2.wireOp",EDGE,"E16.bottom");Q7=makeQuery(id+"F5.boolean.opBoolean","MERGE",FACE,{"derivedFrom":[makeQuery(id+"F3.opExtrude","SWEPT_FACE",FACE,{"disambiguationData":[OSD([subQ0]),TDD([makeQuery(id+"F2.imprint","IMPRINT",EDGE,{"disambiguationData":[TD([[makeQuery(id+"F2.imprint","INTERSECT",VERTEX,{"derivedFrom":[makeQuery(id+"F1.opExtrude","CAP_EDGE",EDGE,{"disambiguationData":[OSD([sQuery(id+"F0.wireOp",EDGE,"E9.right")])],"isStart":false}),subQ0]}),1.0]])],"derivedFrom":subQ0})])]}),makeQuery(id+"F3.opExtrude","SWEPT_FACE",FACE,{"disambiguationData":[OSD([subQ0]),TDD([makeQuery(id+"F2.imprint","IMPRINT",EDGE,{"disambiguationData":[TD([[makeQuery(id+"F2.imprint","INTERSECT",VERTEX,{"derivedFrom":[makeQuery(id+"F1.opExtrude","CAP_EDGE",EDGE,{"disambiguationData":[OSD([sQuery(id+"F0.wireOp",EDGE,"E9.left")])],"isStart":false}),subQ0]}),-1.0]])],"derivedFrom":subQ0})])]}),makeQuery(id+"F3.opExtrude","SWEPT_FACE",FACE,{"disambiguationData":[OSD([subQ0]),TDD([makeQuery(id+"F2.imprint","IMPRINT",EDGE,{"disambiguationData":[TD([[makeQuery(id+"F2.imprint","INTERSECT",VERTEX,{"derivedFrom":[makeQuery(id+"F1.opExtrude","CAP_EDGE",EDGE,{"disambiguationData":[OSD([sQuery(id+"F0.wireOp",EDGE,"E8.left")])],"isStart":false}),subQ0]}),-1.0]])],"derivedFrom":subQ0})])]}),makeQuery(id+"F3.opExtrude","SWEPT_FACE",FACE,{"disambiguationData":[OSD([subQ0]),TDD([makeQuery(id+"F2.imprint","IMPRINT",EDGE,{"disambiguationData":[TD([[makeQuery(id+"F2.imprint","INTERSECT",VERTEX,{"derivedFrom":[makeQuery(id+"F1.opExtrude","CAP_EDGE",EDGE,{"disambiguationData":[OSD([sQuery(id+"F0.wireOp",EDGE,"E7.left")])],"isStart":false}),subQ0]}),-1.0]])],"derivedFrom":subQ0})])]}),makeQuery(id+"F3.opExtrude","SWEPT_FACE",FACE,{"disambiguationData":[OSD([subQ0]),TDD([makeQuery(id+"F2.imprint","IMPRINT",EDGE,{"disambiguationData":[TD([[makeQuery(id+"F2.imprint","INTERSECT",VERTEX,{"derivedFrom":[makeQuery(id+"F1.opExtrude","CAP_EDGE",EDGE,{"disambiguationData":[OSD([sQuery(id+"F0.wireOp",EDGE,"E3.left")])],"isStart":false}),subQ0]}),-1.0]])],"derivedFrom":subQ0})])]}),makeQuery(id+"F3.opExtrude","SWEPT_FACE",FACE,{"disambiguationData":[OSD([subQ0]),TDD([makeQuery(id+"F2.imprint","IMPRINT",EDGE,{"disambiguationData":[TD([[makeQuery(id+"F2.imprint","INTERSECT",VERTEX,{"derivedFrom":[makeQuery(id+"F1.opExtrude","CAP_EDGE",EDGE,{"disambiguationData":[OSD([sQuery(id+"F0.wireOp",EDGE,"E2.left")])],"isStart":false}),subQ0]}),-1.0]])],"derivedFrom":subQ0})])]}),makeQuery(id+"F3.opExtrude","SWEPT_FACE",FACE,{"disambiguationData":[OSD([subQ0]),TDD([makeQuery(id+"F2.imprint","IMPRINT",EDGE,{"disambiguationData":[TD([[makeQuery(id+"F2.imprint","INTERSECT",VERTEX,{"derivedFrom":[makeQuery(id+"F1.opExtrude","CAP_EDGE",EDGE,{"disambiguationData":[OSD([sQuery(id+"F0.wireOp",EDGE,"E1.left")])],"isStart":false}),subQ0]}),-1.0]])],"derivedFrom":subQ0})])]}),makeQuery(id+"F5.opExtrude","SWEPT_FACE",FACE,{"disambiguationData":[OSD([sQuery(id+"F4.wireOp",EDGE,"E17.bottom")])]})]});}
            extrude(context, id + "F18", {"entities" : qUnion([Q0, Q1, Q2, Q3, Q4, Q5, Q6]), "operationType" : NewBodyOperationType.REMOVE, "endBound" : BoundingType.UP_TO_SURFACE, "oppositeDirection" : true, "depth" : 25.4 * mm, "endBoundEntityFace" : qUnion([Q7]), "offsetDistance" : 25.4 * mm});
        }
        {
            var Q0;
            Q0=makeQuery(id+"F7.opExtrude","CAP_EDGE",EDGE,{"disambiguationData":[OSD([sQuery(id+"F6.wireOp",EDGE,"E18.right")])],"isStart":false});
            var Q1;
            Q1=makeQuery(id+"F15.opExtrude","CAP_EDGE",EDGE,{"disambiguationData":[OSD([sQuery(id+"F14.wireOp",EDGE,"E28.left")])],"isStart":false});
            fillet(context, id + "F19", {"entities" : qUnion([Q0, Q1]), "radius" : 3.8 * mm, "tangentPropagation" : true, "allowEdgeOverflow" : false});
        }
    });
